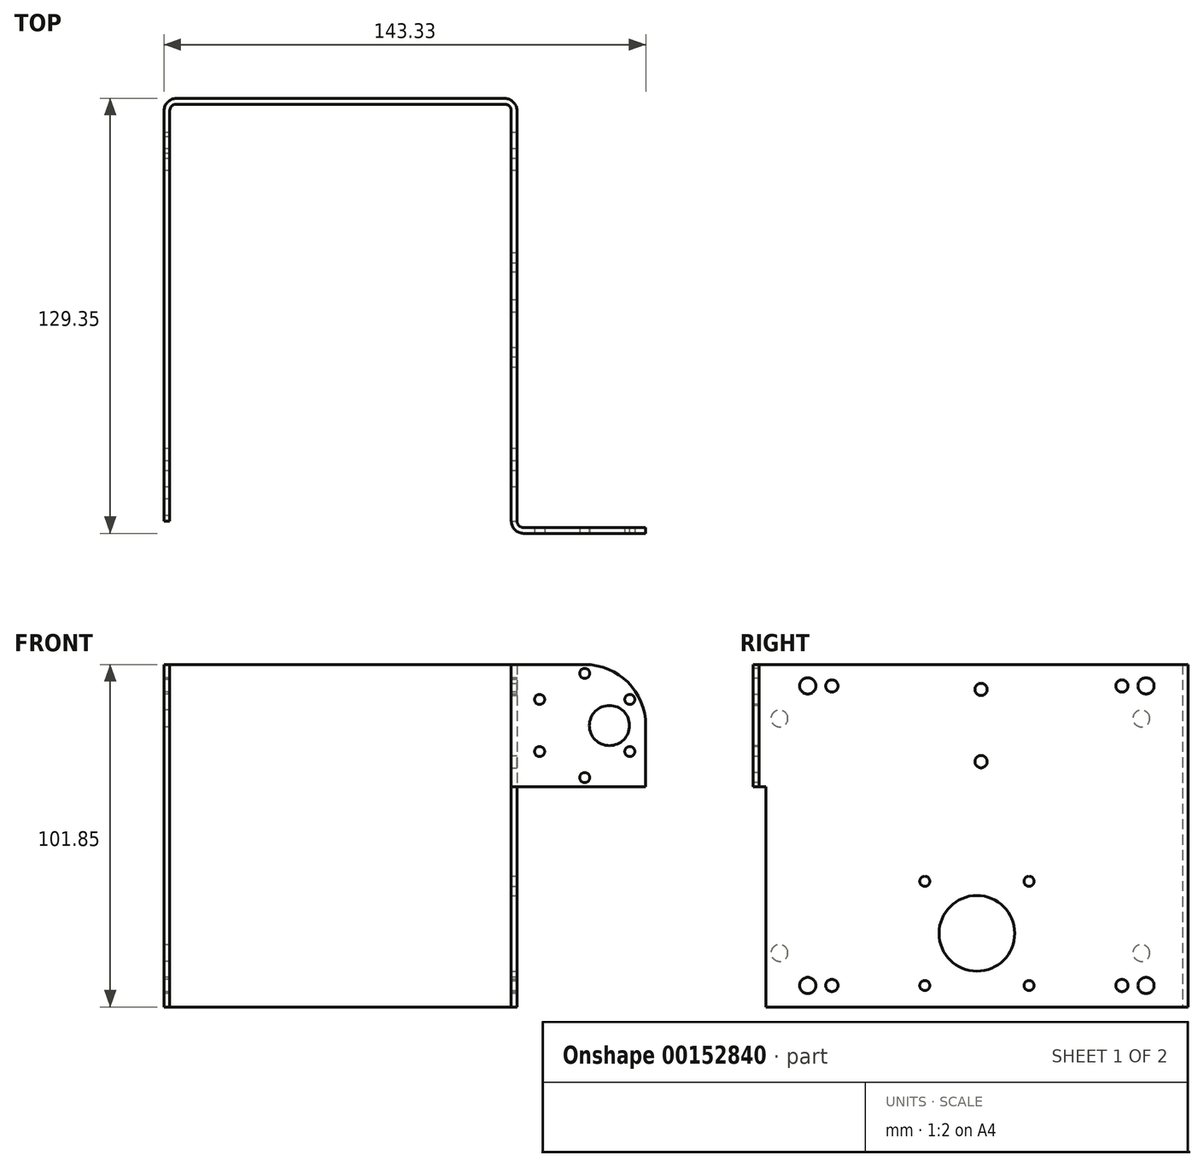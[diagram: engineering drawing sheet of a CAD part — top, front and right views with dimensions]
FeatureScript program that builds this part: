
annotation { "Feature Type Name" : "Feature", "Feature Type Description" : "" }
export const myFeature = defineFeature(function(context is Context, id is Id, definition is map)
    precondition{}
    {
        {
            var Q0;
            Q0=qCreatedBy(makeId("Top.planeOp"),FACE);
            var sketch = newSketch(context, id + "F0", { "sketchPlane" : qUnion([Q0])});
            skLineSegment(sketch, "E0.left", {"start": v(0, 0) * mm, "end": v(0, 123.95) * mm});
            skLineSegment(sketch, "E0.right", {"start": v(-1.7, 0) * mm, "end": v(-1.7, 125.66) * mm});
            skLineSegment(sketch, "E1.bottom", {"start": v(0, 123.95) * mm, "end": v(101.6, 123.95) * mm});
            skLineSegment(sketch, "E1.top", {"start": v(-1.7, 125.66) * mm, "end": v(103.3, 125.66) * mm});
            skLineSegment(sketch, "E2.top", {"start": v(101.6, -3.7) * mm, "end": v(141.62, -3.7) * mm});
            skLineSegment(sketch, "E2.left", {"start": v(101.6, 123.95) * mm, "end": v(101.6, -3.7) * mm});
            skLineSegment(sketch, "E2.right", {"start": v(103.3, 125.66) * mm, "end": v(103.3, -1.98) * mm});
            skLineSegment(sketch, "E3", {"start": v(0, 123.95) * mm, "end": v(-1.7, 123.95) * mm, "construction": true});
            skLineSegment(sketch, "E4", {"start": v(0, 123.95) * mm, "end": v(0, 125.66) * mm, "construction": true});
            skLineSegment(sketch, "E5", {"start": v(101.6, 123.95) * mm, "end": v(103.3, 123.95) * mm, "construction": true});
            skLineSegment(sketch, "E6", {"start": v(101.6, 123.95) * mm, "end": v(101.6, 125.66) * mm, "construction": true});
            skLineSegment(sketch, "E7", {"start": v(103.3, -1.98) * mm, "end": v(141.62, -1.98) * mm});
            skLineSegment(sketch, "E8", {"start": v(141.62, -1.98) * mm, "end": v(141.62, -3.7) * mm});
            skLineSegment(sketch, "E9", {"start": v(0, 0) * mm, "end": v(-1.7, 0) * mm});
            skSolve(sketch);
        }
        {
            var Q0;
            Q0 = qSketchRegion(id + "F0", true);
            extrude(context, id + "F1", {"entities" : qUnion([Q0]), "depth" : 101.85 * mm});
        }
        {
            var Q0;
            Q0=makeQuery(id+"F1.opExtrude","SWEPT_FACE",FACE,{"disambiguationData":[OSD([sQuery(id+"F0.wireOp",EDGE,"E2.top")])]});
            var sketch = newSketch(context, id + "F2", { "sketchPlane" : qUnion([Q0])});
            skLineSegment(sketch, "E10", {"start": v(123.45, 83.7) * mm, "end": v(130.82, 83.7) * mm, "construction": true});
            skCircle(sketch, "E11.cCircle", {"center": v(123.45, 83.7) * mm, "radius": 13.42 * mm, "construction": true});
            skLineSegment(sketch, "E11.0", {"start": v(110.04, 75.95) * mm, "end": v(110.04, 91.44) * mm, "construction": true});
            skLineSegment(sketch, "E11.1", {"start": v(110.04, 91.44) * mm, "end": v(123.45, 99.19) * mm, "construction": true});
            skLineSegment(sketch, "E11.2", {"start": v(123.45, 99.19) * mm, "end": v(136.87, 91.44) * mm, "construction": true});
            skLineSegment(sketch, "E11.3", {"start": v(136.87, 91.44) * mm, "end": v(136.87, 75.95) * mm, "construction": true});
            skLineSegment(sketch, "E11.4", {"start": v(136.87, 75.95) * mm, "end": v(123.45, 68.2) * mm, "construction": true});
            skLineSegment(sketch, "E11.5", {"start": v(123.45, 68.2) * mm, "end": v(110.04, 75.95) * mm, "construction": true});
            skCircle(sketch, "E12", {"center": v(130.82, 83.7) * mm, "radius": 5.97 * mm});
            skCircle(sketch, "E13", {"center": v(136.87, 91.44) * mm, "radius": 1.5 * mm});
            skCircle(sketch, "E14", {"center": v(123.45, 99.19) * mm, "radius": 1.5 * mm});
            skCircle(sketch, "E15", {"center": v(136.87, 75.95) * mm, "radius": 1.5 * mm});
            skCircle(sketch, "E16", {"center": v(123.45, 68.2) * mm, "radius": 1.5 * mm});
            skCircle(sketch, "E17", {"center": v(110.04, 75.95) * mm, "radius": 1.5 * mm});
            skCircle(sketch, "E18", {"center": v(110.04, 91.44) * mm, "radius": 1.5 * mm});
            skLineSegment(sketch, "E19", {"start": v(141.62, 83.7) * mm, "end": v(123.45, 83.7) * mm, "construction": true});
            skLineSegment(sketch, "E20", {"start": v(123.45, 83.7) * mm, "end": v(123.45, 101.85) * mm, "construction": true});
            skSolve(sketch);
        }
        {
            var Q0;
            Q0=makeQuery(id+"F2.imprint","IMPRINT",FACE,{"disambiguationData":[TD([[makeQuery(id+"F2.imprint","IMPRINT",EDGE,{"derivedFrom":sQuery(id+"F2.wireOp",EDGE,"cYeWAqy3-sQsE-WE6J-lgJM-6UOCWVzE8PWo")}),1.0]])]});
            var Q1;
            Q1=makeQuery(id+"F2.imprint","IMPRINT",FACE,{"disambiguationData":[TD([[makeQuery(id+"F2.imprint","IMPRINT",EDGE,{"derivedFrom":sQuery(id+"F2.wireOp",EDGE,"7XhtkfUV-HrZg-TMfK-mJjy-UqklCEwfxlWh")}),1.0]])]});
            var Q2;
            Q2=makeQuery(id+"F2.imprint","IMPRINT",FACE,{"disambiguationData":[TD([[makeQuery(id+"F2.imprint","IMPRINT",EDGE,{"derivedFrom":sQuery(id+"F2.wireOp",EDGE,"MMlwo2rY-IQie-nijV-GMqA-qFSEFU6uMxna")}),1.0]])]});
            var Q3;
            Q3=makeQuery(id+"F2.imprint","IMPRINT",FACE,{"disambiguationData":[TD([[makeQuery(id+"F2.imprint","IMPRINT",EDGE,{"derivedFrom":sQuery(id+"F2.wireOp",EDGE,"zZeZE2kM-HGY1-vqyM-nWvN-wRn4m8AcsAYT")}),1.0]])]});
            var Q4;
            Q4=makeQuery(id+"F2.imprint","IMPRINT",FACE,{"disambiguationData":[TD([[makeQuery(id+"F2.imprint","IMPRINT",EDGE,{"derivedFrom":sQuery(id+"F2.wireOp",EDGE,"TtP8DOI0-ahjF-aBKz-yW09-xlEwp1fkA6Ey")}),1.0]])]});
            var Q5;
            Q5=makeQuery(id+"F2.imprint","IMPRINT",FACE,{"disambiguationData":[TD([[makeQuery(id+"F2.imprint","IMPRINT",EDGE,{"derivedFrom":sQuery(id+"F2.wireOp",EDGE,"vT8ePUNX-NwmP-AFnz-WDrf-PBF7OkZyreDl")}),1.0]])]});
            var Q6;
            Q6=makeQuery(id+"F2.imprint","IMPRINT",FACE,{"disambiguationData":[TD([[makeQuery(id+"F2.imprint","IMPRINT",EDGE,{"derivedFrom":sQuery(id+"F2.wireOp",EDGE,"gStBPKwA-ZJv2-EDWW-pdEw-3KQZwglkEu71")}),1.0]])]});
            var Q7;
            Q7=makeQuery(id+"F2.imprint","IMPRINT",FACE,{"disambiguationData":[TD([[makeQuery(id+"F2.imprint","IMPRINT",EDGE,{"derivedFrom":sQuery(id+"F2.wireOp",EDGE,"E13")}),1.0]])]});
            var Q8;
            Q8=makeQuery(id+"F2.imprint","IMPRINT",FACE,{"disambiguationData":[TD([[makeQuery(id+"F2.imprint","IMPRINT",EDGE,{"derivedFrom":sQuery(id+"F2.wireOp",EDGE,"E12")}),1.0]])]});
            var Q9;
            Q9=makeQuery(id+"F2.imprint","IMPRINT",FACE,{"disambiguationData":[TD([[makeQuery(id+"F2.imprint","IMPRINT",EDGE,{"derivedFrom":sQuery(id+"F2.wireOp",EDGE,"E15")}),1.0]])]});
            var Q10;
            Q10=makeQuery(id+"F2.imprint","IMPRINT",FACE,{"disambiguationData":[TD([[makeQuery(id+"F2.imprint","IMPRINT",EDGE,{"derivedFrom":sQuery(id+"F2.wireOp",EDGE,"E14")}),1.0]])]});
            var Q11;
            Q11=makeQuery(id+"F2.imprint","IMPRINT",FACE,{"disambiguationData":[TD([[makeQuery(id+"F2.imprint","IMPRINT",EDGE,{"derivedFrom":sQuery(id+"F2.wireOp",EDGE,"E18")}),1.0]])]});
            var Q12;
            Q12=makeQuery(id+"F2.imprint","IMPRINT",FACE,{"disambiguationData":[TD([[makeQuery(id+"F2.imprint","IMPRINT",EDGE,{"derivedFrom":sQuery(id+"F2.wireOp",EDGE,"E17")}),1.0]])]});
            var Q13;
            Q13=makeQuery(id+"F2.imprint","IMPRINT",FACE,{"disambiguationData":[TD([[makeQuery(id+"F2.imprint","IMPRINT",EDGE,{"derivedFrom":sQuery(id+"F2.wireOp",EDGE,"E16")}),1.0]])]});
            var Q14;
            Q14=makeQuery(id+"F1.opExtrude","SWEPT_FACE",FACE,{"disambiguationData":[OSD([sQuery(id+"F0.wireOp",EDGE,"E7")])]});
            extrude(context, id + "F3", {"entities" : qUnion([Q0, Q1, Q2, Q3, Q4, Q5, Q6, Q7, Q8, Q9, Q10, Q11, Q12, Q13]), "operationType" : NewBodyOperationType.REMOVE, "endBound" : BoundingType.UP_TO_SURFACE, "oppositeDirection" : true, "endBoundEntityFace" : qUnion([Q14]), "depth" : 25.4 * mm});
        }
        {
            var Q0;
            Q0=makeQuery(id+"F1.opExtrude","SWEPT_EDGE",EDGE,{"disambiguationData":[OSD([sQuery(id+"F0.wireOp",EDGE,"E0.left"),sQuery(id+"F0.wireOp",EDGE,"E1.bottom")])]});
            var Q1;
            Q1=makeQuery(id+"F1.opExtrude","SWEPT_EDGE",EDGE,{"disambiguationData":[OSD([sQuery(id+"F0.wireOp",EDGE,"E1.bottom"),sQuery(id+"F0.wireOp",EDGE,"E2.left")])]});
            var Q2;
            Q2=makeQuery(id+"F1.opExtrude","SWEPT_EDGE",EDGE,{"disambiguationData":[OSD([sQuery(id+"F0.wireOp",EDGE,"E2.right"),sQuery(id+"F0.wireOp",EDGE,"E7")])]});
            fillet(context, id + "F4", {"entities" : qUnion([Q0, Q1, Q2]), "radius" : 1.98 * mm, "tangentPropagation" : true, "allowEdgeOverflow" : false});
        }
        {
            var Q0;
            Q0=makeQuery(id+"F1.opExtrude","SWEPT_EDGE",EDGE,{"disambiguationData":[OSD([sQuery(id+"F0.wireOp",EDGE,"E0.right"),sQuery(id+"F0.wireOp",EDGE,"E1.top")])]});
            var Q1;
            Q1=makeQuery(id+"F1.opExtrude","SWEPT_EDGE",EDGE,{"disambiguationData":[OSD([sQuery(id+"F0.wireOp",EDGE,"E1.top"),sQuery(id+"F0.wireOp",EDGE,"E2.right")])]});
            var Q2;
            Q2=makeQuery(id+"F1.opExtrude","SWEPT_EDGE",EDGE,{"disambiguationData":[OSD([sQuery(id+"F0.wireOp",EDGE,"E2.top"),sQuery(id+"F0.wireOp",EDGE,"E2.left")])]});
            fillet(context, id + "F5", {"entities" : qUnion([Q0, Q1, Q2]), "radius" : 3.7 * mm, "tangentPropagation" : true, "allowEdgeOverflow" : false});
        }
        {
            var Q0;
            Q0=makeQuery(id+"F1.opExtrude","SWEPT_FACE",FACE,{"disambiguationData":[OSD([sQuery(id+"F0.wireOp",EDGE,"E0.right")])]});
            var sketch = newSketch(context, id + "F6", { "sketchPlane" : qUnion([Q0])});
            skLineSegment(sketch, "E21.right", {"start": v(-12.5, 101.85) * mm, "end": v(-12.5, 95.47) * mm, "construction": true});
            skCircle(sketch, "E22", {"center": v(-12.5, 95.47) * mm, "radius": 2.41 * mm});
            skLineSegment(sketch, "E23.bottom", {"start": v(-19.68, 95.47) * mm, "end": v(-105.97, 95.47) * mm, "construction": true});
            skLineSegment(sketch, "E23.top", {"start": v(-19.68, 6.38) * mm, "end": v(-105.97, 6.38) * mm, "construction": true});
            skLineSegment(sketch, "E23.left", {"start": v(-19.68, 95.47) * mm, "end": v(-19.68, 6.38) * mm, "construction": true});
            skLineSegment(sketch, "E23.right", {"start": v(-105.97, 95.47) * mm, "end": v(-105.97, 6.38) * mm, "construction": true});
            skPoint(sketch, "E23.middle", {"position": v(-62.83, 50.93) * mm});
            skLineSegment(sketch, "E24", {"start": v(-19.68, 95.47) * mm, "end": v(-12.5, 95.47) * mm, "construction": true});
            skLineSegment(sketch, "E25", {"start": v(-105.97, 95.47) * mm, "end": v(-113.15, 95.47) * mm, "construction": true});
            skLineSegment(sketch, "E26", {"start": v(-105.97, 6.38) * mm, "end": v(-113.15, 6.38) * mm, "construction": true});
            skLineSegment(sketch, "E27", {"start": v(-19.68, 6.38) * mm, "end": v(-12.5, 6.38) * mm, "construction": true});
            skCircle(sketch, "E28", {"center": v(-19.68, 95.47) * mm, "radius": 1.83 * mm});
            skCircle(sketch, "E29", {"center": v(-105.97, 95.47) * mm, "radius": 1.83 * mm});
            skCircle(sketch, "E30", {"center": v(-105.97, 6.38) * mm, "radius": 1.83 * mm});
            skCircle(sketch, "E31", {"center": v(-19.68, 6.38) * mm, "radius": 1.83 * mm});
            skCircle(sketch, "E32", {"center": v(-113.15, 95.47) * mm, "radius": 2.41 * mm});
            skCircle(sketch, "E33", {"center": v(-113.15, 6.38) * mm, "radius": 2.41 * mm});
            skCircle(sketch, "E34", {"center": v(-12.5, 6.38) * mm, "radius": 2.41 * mm});
            skLineSegment(sketch, "E35", {"start": v(-62.83, 50.93) * mm, "end": v(0, 50.93) * mm, "construction": true});
            skLineSegment(sketch, "E36", {"start": v(-113.15, 95.47) * mm, "end": v(-123.95, 95.47) * mm, "construction": true});
            skSolve(sketch);
        }
        {
            var Q0;
            Q0 = qSketchRegion(id + "F6", true);
            var Q1;
            Q1=makeQuery(id+"F1.opExtrude","SWEPT_FACE",FACE,{"disambiguationData":[OSD([sQuery(id+"F0.wireOp",EDGE,"E2.right")])]});
            extrude(context, id + "F7", {"entities" : qUnion([Q0]), "operationType" : NewBodyOperationType.REMOVE, "endBound" : BoundingType.UP_TO_SURFACE, "oppositeDirection" : true, "endBoundEntityFace" : qUnion([Q1]), "depth" : 25.4 * mm});
        }
        {
            var Q0;
            Q0=makeQuery(id+"F1.opExtrude","SWEPT_FACE",FACE,{"disambiguationData":[OSD([sQuery(id+"F0.wireOp",EDGE,"E2.right")])]});
            var sketch = newSketch(context, id + "F8", { "sketchPlane" : qUnion([Q0])});
            skPoint(sketch, "E37.middle", {"position": v(62.83, 21.88) * mm});
            skLineSegment(sketch, "E38.bottom", {"start": v(78.33, 6.38) * mm, "end": v(47.33, 6.38) * mm, "construction": true});
            skLineSegment(sketch, "E38.top", {"start": v(78.33, 37.38) * mm, "end": v(47.33, 37.38) * mm, "construction": true});
            skLineSegment(sketch, "E38.left", {"start": v(78.33, 6.38) * mm, "end": v(78.33, 37.38) * mm, "construction": true});
            skLineSegment(sketch, "E38.right", {"start": v(47.33, 6.38) * mm, "end": v(47.33, 37.38) * mm, "construction": true});
            skCircle(sketch, "E39", {"center": v(62.83, 21.88) * mm, "radius": 11.25 * mm});
            skCircle(sketch, "E40", {"center": v(47.33, 37.38) * mm, "radius": 1.5 * mm});
            skCircle(sketch, "E41", {"center": v(78.33, 37.38) * mm, "radius": 1.5 * mm});
            skCircle(sketch, "E42", {"center": v(78.33, 6.38) * mm, "radius": 1.5 * mm});
            skCircle(sketch, "E43", {"center": v(47.33, 6.38) * mm, "radius": 1.5 * mm});
            skLineSegment(sketch, "E44", {"start": v(-1.98, 83.7) * mm, "end": v(64.06, 83.7) * mm, "construction": true});
            skLineSegment(sketch, "E45", {"start": v(64.06, 72.95) * mm, "end": v(64.06, 94.44) * mm, "construction": true});
            skCircle(sketch, "E46", {"center": v(64.06, 72.95) * mm, "radius": 1.83 * mm});
            skCircle(sketch, "E47", {"center": v(64.06, 94.44) * mm, "radius": 1.83 * mm});
            skLineSegment(sketch, "E48", {"start": v(19.68, 6.38) * mm, "end": v(47.33, 6.38) * mm, "construction": true});
            skLineSegment(sketch, "E49", {"start": v(105.97, 6.38) * mm, "end": v(78.33, 6.38) * mm, "construction": true});
            skSolve(sketch);
        }
        {
            var Q0;
            Q0 = qSketchRegion(id + "F8", true);
            var Q1;
            Q1=makeQuery(id+"F1.opExtrude","SWEPT_FACE",FACE,{"disambiguationData":[OSD([sQuery(id+"F0.wireOp",EDGE,"E0.left")])]});
            extrude(context, id + "F9", {"entities" : qUnion([Q0]), "operationType" : NewBodyOperationType.REMOVE, "endBound" : BoundingType.UP_TO_SURFACE, "oppositeDirection" : true, "endBoundEntityFace" : qUnion([Q1]), "depth" : 25.4 * mm});
        }
        {
            var Q0;
            Q0=makeQuery(id+"F1.opExtrude","SWEPT_FACE",FACE,{"disambiguationData":[OSD([sQuery(id+"F0.wireOp",EDGE,"E8")])]});
            var sketch = newSketch(context, id + "F10", { "sketchPlane" : qUnion([Q0])});
            skLineSegment(sketch, "E50.bottom", {"start": v(-3.7, 0) * mm, "end": v(0, 0) * mm});
            skLineSegment(sketch, "E50.top", {"start": v(-3.7, 65.53) * mm, "end": v(0, 65.53) * mm});
            skLineSegment(sketch, "E50.left", {"start": v(-3.7, 0) * mm, "end": v(-3.7, 65.53) * mm});
            skLineSegment(sketch, "E50.right", {"start": v(0, 0) * mm, "end": v(0, 65.53) * mm});
            skLineSegment(sketch, "E51", {"start": v(-3.7, 65.53) * mm, "end": v(-3.7, 83.7) * mm, "construction": true});
            skLineSegment(sketch, "E52", {"start": v(-3.7, 83.7) * mm, "end": v(-3.7, 101.85) * mm, "construction": true});
            skSolve(sketch);
        }
        {
            var Q0;
            Q0 = qSketchRegion(id + "F10", true);
            var Q1;
            Q1=makeQuery(id+"F1.opExtrude","SWEPT_FACE",FACE,{"disambiguationData":[OSD([sQuery(id+"F0.wireOp",EDGE,"E2.left")])]});
            extrude(context, id + "F11", {"entities" : qUnion([Q0]), "operationType" : NewBodyOperationType.REMOVE, "endBound" : BoundingType.UP_TO_SURFACE, "oppositeDirection" : true, "endBoundEntityFace" : qUnion([Q1]), "depth" : 25.4 * mm});
        }
        {
            var Q0;
            Q0=makeQuery(id+"FueQOPK2oRYlmx7_1.boolean.opBoolean","COPY",EDGE,{"derivedFrom":makeQuery(id+"FueQOPK2oRYlmx7_1.opExtrude","CAP_EDGE",EDGE,{"disambiguationData":[OSD([sQuery(id+"FlpDpRoYcaPuYPA_1.wireOp",EDGE,"j9SRtD0E-Qv5I-qyEs-LzdI-TA50SBaRRNv9.top")])],"isStart":true})});
            var Q1;
            Q1=makeQuery(id+"FueQOPK2oRYlmx7_1.boolean.opBoolean","COPY",EDGE,{"derivedFrom":makeQuery(id+"FueQOPK2oRYlmx7_1.opExtrude","CAP_EDGE",EDGE,{"disambiguationData":[OSD([sQuery(id+"FlpDpRoYcaPuYPA_1.wireOp",EDGE,"nwioXLwu-Ot8Y-8ZOU-BmCs-KjH4GpdfyhlB.top")])],"isStart":true})});
            var Q2;
            {var subQ0=sQuery(id+"FlpDpRoYcaPuYPA_1.wireOp",EDGE,"nwioXLwu-Ot8Y-8ZOU-BmCs-KjH4GpdfyhlB.top");var subQ1=sQuery(id+"F0.wireOp",EDGE,"cnXe6Naq-0nZv-2cTg-ID4I-fOnZyj1EtF48.right");var subQ2=makeQuery(id+"FlpDpRoYcaPuYPA_1.imprint","INTERSECT",VERTEX,{"derivedFrom":[makeQuery(id+"F1.opExtrude","SWEPT_EDGE",EDGE,{"disambiguationData":[OSD([sQuery(id+"F0.wireOp",EDGE,"cnXe6Naq-0nZv-2cTg-ID4I-fOnZyj1EtF48.top"),subQ1])]}),subQ0]});Q2=makeQuery(id+"FueQOPK2oRYlmx7_1.boolean.opBoolean","COPY",EDGE,{"derivedFrom":makeQuery(id+"FueQOPK2oRYlmx7_1.opExtrude","TWEAK_EDGE",EDGE,{"derivedFrom":[makeQuery(id+"F1.opExtrude","SWEPT_FACE",FACE,{"disambiguationData":[OSD([sQuery(id+"F0.wireOp",EDGE,"E8")])]}),makeQuery(id+"FlpDpRoYcaPuYPA_1.imprint","IMPRINT",EDGE,{"disambiguationData":[TD([[subQ2,1.0]])],"derivedFrom":subQ0}),makeQuery(id+"FlpDpRoYcaPuYPA_1.imprint","IMPRINT",EDGE,{"disambiguationData":[TD([[makeQuery(id+"FlpDpRoYcaPuYPA_1.imprint","INTERSECT",VERTEX,{"derivedFrom":[subQ0,sQuery(id+"FlpDpRoYcaPuYPA_1.wireOp",EDGE,"nwioXLwu-Ot8Y-8ZOU-BmCs-KjH4GpdfyhlB.right")]}),1.0]])],"derivedFrom":subQ0})]})});}
            var Q3;
            {var subQ0=sQuery(id+"FlpDpRoYcaPuYPA_1.wireOp",EDGE,"j9SRtD0E-Qv5I-qyEs-LzdI-TA50SBaRRNv9.top");var subQ1=sQuery(id+"F0.wireOp",EDGE,"cnXe6Naq-0nZv-2cTg-ID4I-fOnZyj1EtF48.right");var subQ2=makeQuery(id+"FlpDpRoYcaPuYPA_1.imprint","INTERSECT",VERTEX,{"derivedFrom":[makeQuery(id+"F1.opExtrude","SWEPT_EDGE",EDGE,{"disambiguationData":[OSD([sQuery(id+"F0.wireOp",EDGE,"cnXe6Naq-0nZv-2cTg-ID4I-fOnZyj1EtF48.top"),subQ1])]}),subQ0]});Q3=makeQuery(id+"FueQOPK2oRYlmx7_1.boolean.opBoolean","COPY",EDGE,{"derivedFrom":makeQuery(id+"FueQOPK2oRYlmx7_1.opExtrude","TWEAK_EDGE",EDGE,{"derivedFrom":[makeQuery(id+"F1.opExtrude","SWEPT_FACE",FACE,{"disambiguationData":[OSD([sQuery(id+"F0.wireOp",EDGE,"E8")])]}),makeQuery(id+"FlpDpRoYcaPuYPA_1.imprint","IMPRINT",EDGE,{"disambiguationData":[TD([[subQ2,1.0]])],"derivedFrom":subQ0}),makeQuery(id+"FlpDpRoYcaPuYPA_1.imprint","IMPRINT",EDGE,{"disambiguationData":[TD([[makeQuery(id+"FlpDpRoYcaPuYPA_1.imprint","INTERSECT",VERTEX,{"derivedFrom":[subQ0,sQuery(id+"FlpDpRoYcaPuYPA_1.wireOp",EDGE,"j9SRtD0E-Qv5I-qyEs-LzdI-TA50SBaRRNv9.right")]}),1.0]])],"derivedFrom":subQ0})]})});}
            var Q4;
            Q4=makeQuery(id+"F11.boolean.opBoolean","COPY",EDGE,{"derivedFrom":makeQuery(id+"F11.opExtrude","CAP_EDGE",EDGE,{"disambiguationData":[OSD([sQuery(id+"F10.wireOp",EDGE,"E50.top")])],"isStart":true})});
            var Q5;
            Q5=makeQuery(id+"F1.opExtrude","CAP_EDGE",EDGE,{"disambiguationData":[OSD([sQuery(id+"F0.wireOp",EDGE,"E8")])],"isStart":false});
            fillet(context, id + "F12", {"entities" : qUnion([Q0, Q1, Q2, Q3, Q4, Q5]), "radius" : 18.16 * mm, "tangentPropagation" : true, "allowEdgeOverflow" : false});
        }
        {
            var Q0;
            Q0=makeQuery(id+"F1.opExtrude","SWEPT_FACE",FACE,{"disambiguationData":[OSD([sQuery(id+"F0.wireOp",EDGE,"E0.right")])]});
            var sketch = newSketch(context, id + "F13", { "sketchPlane" : qUnion([Q0])});
            skLineSegment(sketch, "E53", {"start": v(0, 50.93) * mm, "end": v(-4.09, 50.93) * mm, "construction": true});
            skLineSegment(sketch, "E54.bottom", {"start": v(-111.75, 16.06) * mm, "end": v(-4.09, 16.06) * mm, "construction": true});
            skLineSegment(sketch, "E54.top", {"start": v(-111.75, 85.8) * mm, "end": v(-4.09, 85.8) * mm, "construction": true});
            skLineSegment(sketch, "E54.left", {"start": v(-111.75, 16.06) * mm, "end": v(-111.75, 85.8) * mm, "construction": true});
            skLineSegment(sketch, "E54.right", {"start": v(-4.09, 16.06) * mm, "end": v(-4.09, 85.8) * mm, "construction": true});
            skCircle(sketch, "E55", {"center": v(-111.75, 16.06) * mm, "radius": 2.5 * mm});
            skCircle(sketch, "E56", {"center": v(-4.09, 16.06) * mm, "radius": 2.5 * mm});
            skCircle(sketch, "E57", {"center": v(-4.09, 85.8) * mm, "radius": 2.5 * mm});
            skCircle(sketch, "E58", {"center": v(-111.75, 85.8) * mm, "radius": 2.5 * mm});
            skSolve(sketch);
        }
        {
            var Q0;
            Q0 = qSketchRegion(id + "F13", true);
            var Q1;
            Q1=makeQuery(id+"F1.opExtrude","SWEPT_FACE",FACE,{"disambiguationData":[OSD([sQuery(id+"F0.wireOp",EDGE,"E0.left")])]});
            extrude(context, id + "F14", {"entities" : qUnion([Q0]), "operationType" : NewBodyOperationType.REMOVE, "endBound" : BoundingType.UP_TO_SURFACE, "oppositeDirection" : true, "endBoundEntityFace" : qUnion([Q1]), "depth" : 25.4 * mm});
        }
    });
